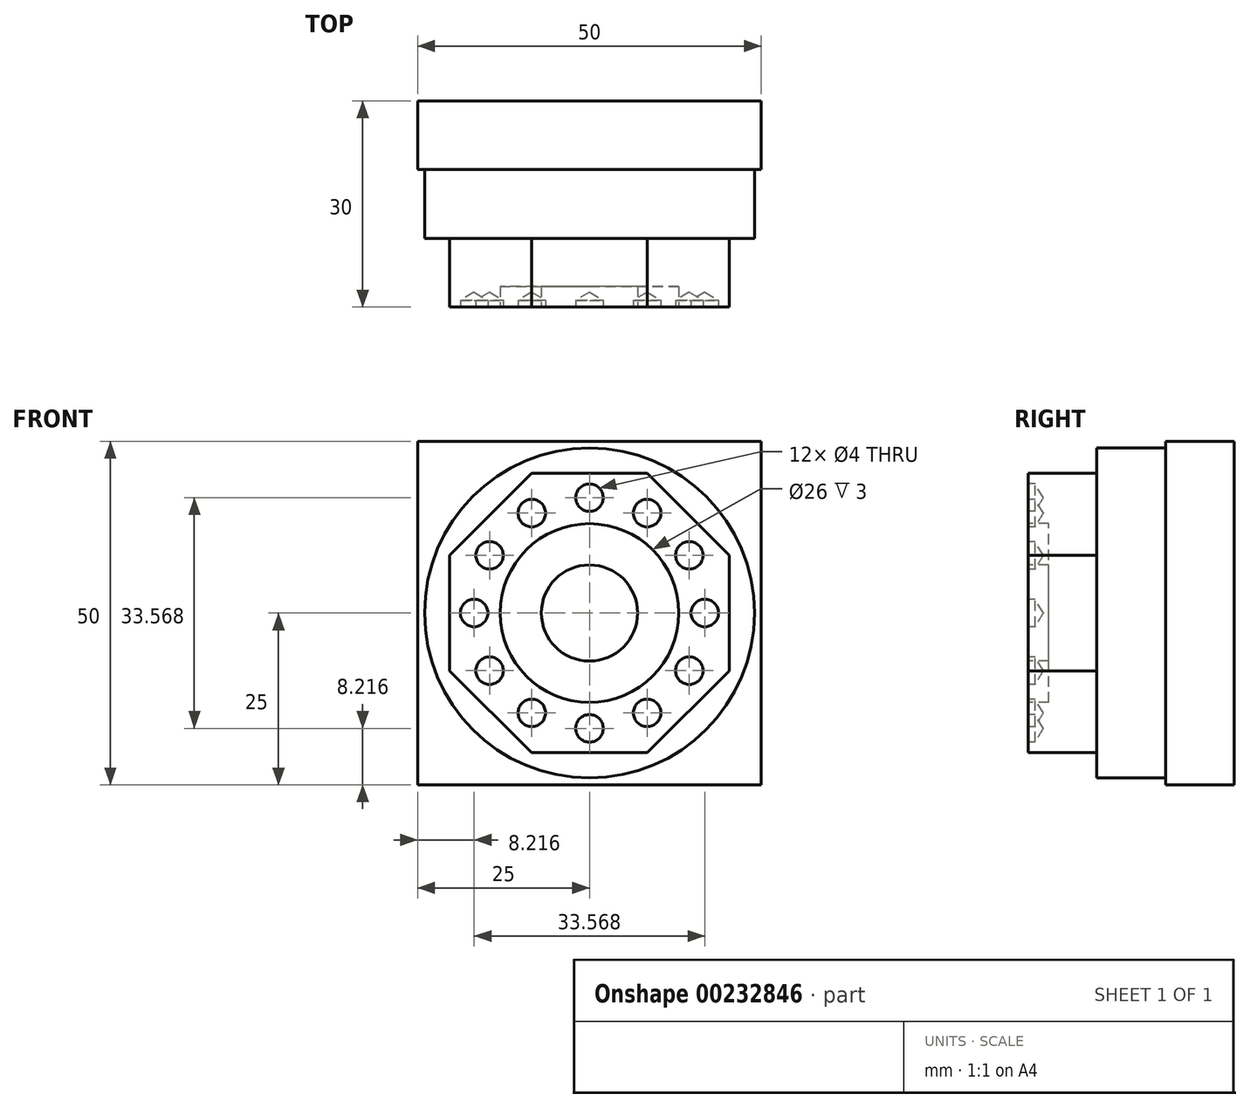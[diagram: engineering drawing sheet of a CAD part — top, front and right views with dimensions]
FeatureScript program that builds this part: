
annotation { "Feature Type Name" : "Feature", "Feature Type Description" : "" }
export const myFeature = defineFeature(function(context is Context, id is Id, definition is map)
    precondition{}
    {
        {
            var Q0;
            Q0=qCreatedBy(makeId("Front.planeOp"),FACE);
            var sketch = newSketch(context, id + "F0", { "sketchPlane" : qUnion([Q0])});
            skLineSegment(sketch, "E0.bottom", {"start": v(-25, 25) * mm, "end": v(25, 25) * mm});
            skLineSegment(sketch, "E0.top", {"start": v(-25, -25) * mm, "end": v(25, -25) * mm});
            skLineSegment(sketch, "E0.left", {"start": v(-25, 25) * mm, "end": v(-25, -25) * mm});
            skLineSegment(sketch, "E0.right", {"start": v(25, 25) * mm, "end": v(25, -25) * mm});
            skPoint(sketch, "E1.endSnap0", {"position": v(0, 25) * mm});
            skPoint(sketch, "E1.end.orphan", {"position": v(0, 25) * mm});
            skSolve(sketch);
        }
        {
            var Q0;
            Q0 = qSketchRegion(id + "F0", true);
            extrude(context, id + "F1", {"entities" : qUnion([Q0]), "depth" : 10 * mm});
        }
        {
            var Q0;
            Q0=makeQuery(id+"F1.opExtrude","CAP_FACE",FACE,{"disambiguationData":[OSD([sQuery(id+"F0.wireOp",EDGE,"E0.bottom"),sQuery(id+"F0.wireOp",EDGE,"E0.top"),sQuery(id+"F0.wireOp",EDGE,"E0.left"),sQuery(id+"F0.wireOp",EDGE,"E0.right")])],"isStart":false});
            var sketch = newSketch(context, id + "F2", { "sketchPlane" : qUnion([Q0])});
            skCircle(sketch, "E2", {"center": v(0, 0) * mm, "radius": 24 * mm});
            skSolve(sketch);
        }
        {
            var Q0;
            Q0=makeQuery(id+"F2.imprint","IMPRINT",FACE,{"disambiguationData":[TD([[makeQuery(id+"F2.imprint","IMPRINT",EDGE,{"derivedFrom":sQuery(id+"F2.wireOp",EDGE,"E2")}),1.0]])]});
            extrude(context, id + "F3", {"entities" : qUnion([Q0]), "operationType" : NewBodyOperationType.ADD, "depth" : 10 * mm});
        }
        {
            var Q0;
            Q0=makeQuery(id+"F3.opExtrude","CAP_FACE",FACE,{"disambiguationData":[OSD([sQuery(id+"F2.wireOp",EDGE,"E2")])],"isStart":false});
            var sketch = newSketch(context, id + "F4", { "sketchPlane" : qUnion([Q0])});
            skCircle(sketch, "E3.cCircle", {"center": v(0, 0) * mm, "radius": 22 * mm, "construction": true});
            skLineSegment(sketch, "E4", {"start": v(0, 20.32) * mm, "end": v(0, 20.34) * mm});
            skLineSegment(sketch, "E5.0", {"start": v(8.42, 20.32) * mm, "end": v(20.33, 8.42) * mm});
            skLineSegment(sketch, "E5.1", {"start": v(20.32, 8.42) * mm, "end": v(20.32, -8.42) * mm});
            skLineSegment(sketch, "E5.2", {"start": v(20.32, -8.42) * mm, "end": v(8.42, -20.33) * mm});
            skLineSegment(sketch, "E5.3", {"start": v(8.42, -20.32) * mm, "end": v(-8.42, -20.32) * mm});
            skLineSegment(sketch, "E5.4", {"start": v(-8.42, -20.32) * mm, "end": v(-20.32, -8.42) * mm});
            skLineSegment(sketch, "E5.5", {"start": v(-20.32, -8.42) * mm, "end": v(-20.32, 8.42) * mm});
            skLineSegment(sketch, "E5.6", {"start": v(-20.32, 8.42) * mm, "end": v(-8.42, 20.33) * mm});
            skLineSegment(sketch, "E5.7", {"start": v(-8.42, 20.33) * mm, "end": v(8.42, 20.32) * mm});
            skSolve(sketch);
        }
        {
            var Q0;
            {var subQ1=sQuery(id+"F4.wireOp",EDGE,"E5.0");Q0=makeQuery(id+"F4.imprint","IMPRINT",FACE,{"disambiguationData":[TD([[makeQuery(id+"F4.imprint","IMPRINT",EDGE,{"derivedFrom":subQ1}),-1.0]])]});}
            extrude(context, id + "F5", {"entities" : qUnion([Q0]), "operationType" : NewBodyOperationType.ADD, "depth" : 10 * mm});
        }
        {
            var Q0;
            Q0=makeQuery(id+"F5.opExtrude","CAP_FACE",FACE,{"disambiguationData":[OSD([sQuery(id+"F4.wireOp",EDGE,"E5.0"),sQuery(id+"F4.wireOp",EDGE,"E5.1"),sQuery(id+"F4.wireOp",EDGE,"E5.2"),sQuery(id+"F4.wireOp",EDGE,"E5.3"),sQuery(id+"F4.wireOp",EDGE,"E5.4"),sQuery(id+"F4.wireOp",EDGE,"E5.5"),sQuery(id+"F4.wireOp",EDGE,"E5.6"),sQuery(id+"F4.wireOp",EDGE,"E5.7")])],"isStart":false});
            var sketch = newSketch(context, id + "F6", { "sketchPlane" : qUnion([Q0])});
            skCircle(sketch, "E6", {"center": v(8.4, 14.54) * mm, "radius": 2.5 * mm});
            skCircle(sketch, "E7.1.0", {"center": v(0, 16.78) * mm, "radius": 2.5 * mm});
            skCircle(sketch, "E7.2.0", {"center": v(-8.4, 14.54) * mm, "radius": 2.5 * mm});
            skCircle(sketch, "E7.3.0", {"center": v(-14.54, 8.4) * mm, "radius": 2.5 * mm});
            skCircle(sketch, "E7.4.0", {"center": v(-16.78, 0) * mm, "radius": 2.5 * mm});
            skCircle(sketch, "E7.5.0", {"center": v(-14.54, -8.4) * mm, "radius": 2.5 * mm});
            skCircle(sketch, "E7.6.0", {"center": v(-8.4, -14.54) * mm, "radius": 2.5 * mm});
            skCircle(sketch, "E7.7.0", {"center": v(0, -16.78) * mm, "radius": 2.5 * mm});
            skCircle(sketch, "E7.8.0", {"center": v(8.4, -14.54) * mm, "radius": 2.5 * mm});
            skCircle(sketch, "E7.9.0", {"center": v(14.54, -8.4) * mm, "radius": 2.5 * mm});
            skCircle(sketch, "E7.10.0", {"center": v(16.78, 0) * mm, "radius": 2.5 * mm});
            skCircle(sketch, "E7.11.0", {"center": v(14.54, 8.4) * mm, "radius": 2.5 * mm});
            skPoint(sketch, "E7.center", {"position": v(0, 0) * mm});
            skLineSegment(sketch, "E8", {"start": v(16.78, 0) * mm, "end": v(17.26, 0) * mm});
            skSolve(sketch);
        }
        {
            var Q0;
            Q0=sQuery(id+"F6.wireOp",VERTEX,"E7.2.0.center");
            var Q1;
            Q1=sQuery(id+"F6.wireOp",VERTEX,"E7.1.0.center");
            var Q2;
            Q2=sQuery(id+"F6.wireOp",VERTEX,"E6.center");
            var Q3;
            Q3=sQuery(id+"F6.wireOp",VERTEX,"E7.11.0.center");
            var Q4;
            Q4=sQuery(id+"F6.wireOp",VERTEX,"E8.start");
            var Q5;
            Q5=sQuery(id+"F6.wireOp",VERTEX,"E7.9.0.center");
            var Q6;
            Q6=sQuery(id+"F6.wireOp",VERTEX,"E7.8.0.center");
            var Q7;
            Q7=sQuery(id+"F6.wireOp",VERTEX,"E7.7.0.center");
            var Q8;
            Q8=sQuery(id+"F6.wireOp",VERTEX,"E7.6.0.center");
            var Q9;
            Q9=sQuery(id+"F6.wireOp",VERTEX,"E7.5.0.center");
            var Q10;
            Q10=sQuery(id+"F6.wireOp",VERTEX,"E7.4.0.center");
            var Q11;
            Q11=sQuery(id+"F6.wireOp",VERTEX,"E7.3.0.center");
            var Q12;
            Q12=makeQuery(id+"F1.opExtrude","SWEPT_BODY",BODY,{"disambiguationData":[OSD([sQuery(id+"F0.wireOp",EDGE,"E0.bottom"),sQuery(id+"F0.wireOp",EDGE,"E0.top"),sQuery(id+"F0.wireOp",EDGE,"E0.left"),sQuery(id+"F0.wireOp",EDGE,"E0.right")])]});
            hole(context, id + "F7", {"style" : HoleStyle.SIMPLE, "endStyle" : HoleEndStyle.BLIND, "holeDiameter" : 4 * mm, "holeDepth" : 1 * mm, "locations" : qUnion([Q0, Q1, Q2, Q3, Q4, Q5, Q6, Q7, Q8, Q9, Q10, Q11]), "scope" : qUnion([Q12]), "tappedDepth" : 12 * mm, "tapClearance" : 3});
        }
        {
            var Q0;
            Q0=makeQuery(id+"F5.opExtrude","CAP_FACE",FACE,{"disambiguationData":[OSD([sQuery(id+"F4.wireOp",EDGE,"E5.0"),sQuery(id+"F4.wireOp",EDGE,"E5.1"),sQuery(id+"F4.wireOp",EDGE,"E5.2"),sQuery(id+"F4.wireOp",EDGE,"E5.3"),sQuery(id+"F4.wireOp",EDGE,"E5.4"),sQuery(id+"F4.wireOp",EDGE,"E5.5"),sQuery(id+"F4.wireOp",EDGE,"E5.6"),sQuery(id+"F4.wireOp",EDGE,"E5.7")])],"isStart":false});
            var sketch = newSketch(context, id + "F8", { "sketchPlane" : qUnion([Q0])});
            skCircle(sketch, "E9", {"center": v(0, 0) * mm, "radius": 7 * mm});
            skCircle(sketch, "E10", {"center": v(0, 0) * mm, "radius": 13 * mm});
            skSolve(sketch);
        }
        {
            var Q0;
            Q0=makeQuery(id+"F8.imprint","IMPRINT",FACE,{"disambiguationData":[TD([[makeQuery(id+"F8.imprint","IMPRINT",EDGE,{"derivedFrom":sQuery(id+"F8.wireOp",EDGE,"E9")}),-1.0]])]});
            extrude(context, id + "F9", {"entities" : qUnion([Q0]), "operationType" : NewBodyOperationType.REMOVE, "oppositeDirection" : true, "depth" : 3 * mm});
        }
    });
